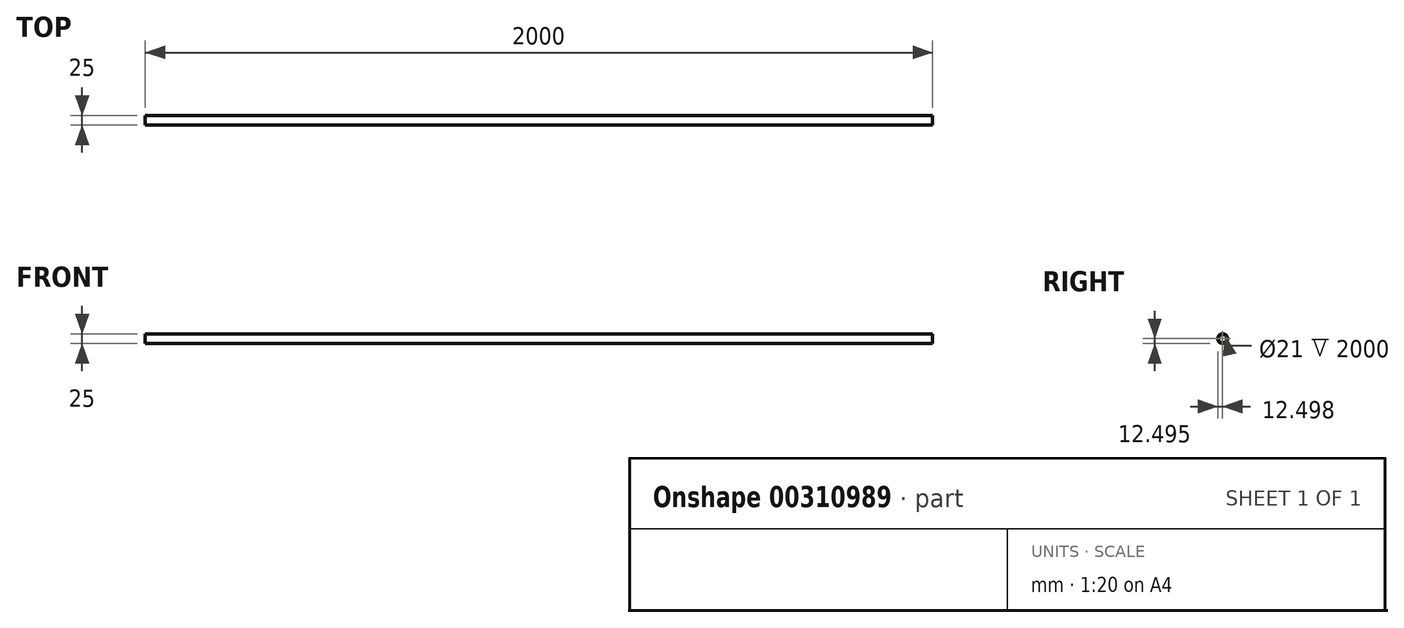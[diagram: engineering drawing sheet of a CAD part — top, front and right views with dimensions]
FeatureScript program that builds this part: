
annotation { "Feature Type Name" : "Feature", "Feature Type Description" : "" }
export const myFeature = defineFeature(function(context is Context, id is Id, definition is map)
    precondition{}
    {
        {
            var Q0;
            Q0=qCreatedBy(makeId("Right.planeOp"),FACE);
            var sketch = newSketch(context, id + "F0", { "sketchPlane" : qUnion([Q0])});
            skCircle(sketch, "E0", {"center": v(-27.82, 18.27) * mm, "radius": 12.5 * mm});
            skCircle(sketch, "E1", {"center": v(-27.82, 18.27) * mm, "radius": 10.5 * mm});
            skSolve(sketch);
        }
        {
            var Q0;
            Q0=makeQuery(id+"F0.imprint","IMPRINT",FACE,{"disambiguationData":[TD([[makeQuery(id+"F0.imprint","IMPRINT",EDGE,{"derivedFrom":sQuery(id+"F0.wireOp",EDGE,"E0")}),1.0]])]});
            extrude(context, id + "F1", {"entities" : qUnion([Q0]), "depth" : 2000 * mm});
        }
    });
